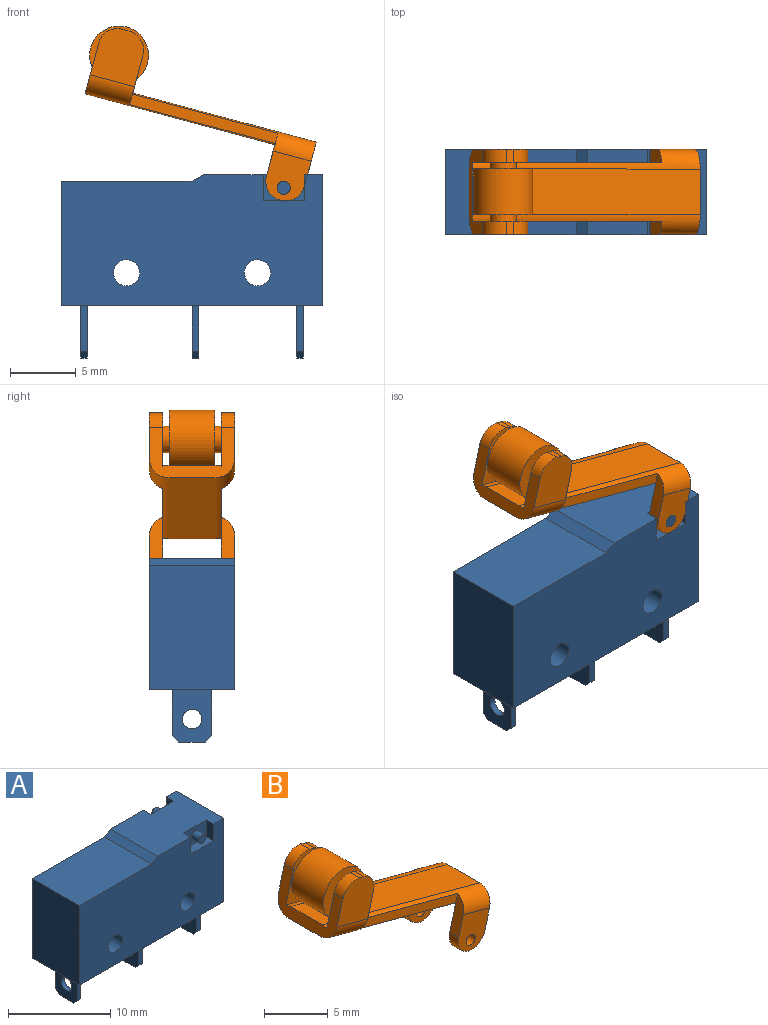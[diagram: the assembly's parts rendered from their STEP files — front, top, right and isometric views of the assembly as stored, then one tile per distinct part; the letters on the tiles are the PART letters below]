
ASSEMBLY  parts=2 mates=1
PART A: 46 faces, bbox 20x6.5x14 mm
  f0: plane 20x10mm, normal (0,1,0), area 182.2mm2, adj f2,f3,f4,f5,f6,f7,f8,f9
  f1: plane 20x10mm, normal (0,-1,0), area 182.2mm2, adj f2,f3,f4,f5,f6,f7,f8,f9
  f2: plane 20x6.5mm, normal (0,0,-1), area 125.5mm2, adj f0,f1,f6,f9,f10,f12,f13,f14
  f3: plane 9.13x6.5mm, normal (0,0,1), area 53.1mm2, adj f0,f1,f4,f9,f34,f35,f38,f40
  f4: plane 6.5x0.87mm, normal (-0.5,0,0.87), area 6.5mm2, adj f0,f1,f3,f5
  f5: plane 10x6.5mm, normal (0,0,1), area 65mm2, adj f0,f1,f4,f6
  f6: plane 9.5x6.5mm, normal (-1,0,0), area 61.8mm2, adj f0,f1,f2,f5
  f7: cylinder r=1mm len=6.5mm, axis (0,1,0), area 40.8mm2, adj f0,f1
  f8: cylinder r=1mm len=6.5mm, axis (0,1,0), area 40.8mm2, adj f0,f1
  f9: plane 10x6.5mm, normal (1,0,0), area 65mm2, adj f0,f1,f2,f3
  f10: plane 4x3mm, normal (-1,0,0), area 10mm2, adj f2,f11,f13,f14,f27,f30,f33
  f11: plane 2x0.5mm, normal (0,0,-1), area 1mm2, adj f10,f12,f30,f33
  f12: plane 4x3mm, normal (1,0,0), area 10mm2, adj f2,f11,f13,f14,f27,f30,f33
  f13: plane 3.5x0.5mm, normal (0,-1,0), area 1.8mm2, adj f2,f10,f12,f33
  f14: plane 3.5x0.5mm, normal (0,1,0), area 1.8mm2, adj f2,f10,f12,f30
  f15: plane 4x3mm, normal (-1,0,0), area 10mm2, adj f2,f16,f18,f19,f26,f29,f32
  f16: plane 2x0.5mm, normal (0,0,-1), area 1mm2, adj f15,f17,f29,f32
  f17: plane 4x3mm, normal (1,0,0), area 10mm2, adj f2,f16,f18,f19,f26,f29,f32
  f18: plane 3.5x0.5mm, normal (0,-1,0), area 1.8mm2, adj f2,f15,f17,f32
  f19: plane 3.5x0.5mm, normal (0,1,0), area 1.8mm2, adj f2,f15,f17,f29
  f20: plane 4x3mm, normal (-1,0,0), area 10mm2, adj f2,f21,f23,f24,f25,f28,f31
  f21: plane 2x0.5mm, normal (0,0,-1), area 1mm2, adj f20,f22,f28,f31
  f22: plane 4x3mm, normal (1,0,0), area 10mm2, adj f2,f21,f23,f24,f25,f28,f31
  f23: plane 3.5x0.5mm, normal (0,-1,0), area 1.8mm2, adj f2,f20,f22,f31
  f24: plane 3.5x0.5mm, normal (0,1,0), area 1.8mm2, adj f2,f20,f22,f28
  f25: cylinder r=0.75mm len=1.5mm, axis (-1,0,0), area 2.4mm2, adj f20,f22
  f26: cylinder r=0.75mm len=1.5mm, axis (-1,0,0), area 2.4mm2, adj f15,f17
  f27: cylinder r=0.75mm len=1.5mm, axis (-1,0,0), area 2.4mm2, adj f10,f12
  f28: plane 0.5x0.5mm, normal (0,0.71,-0.71), area 0.4mm2, adj f20,f21,f22,f24
  f29: plane 0.5x0.5mm, normal (0,0.71,-0.71), area 0.4mm2, adj f15,f16,f17,f19
  f30: plane 0.5x0.5mm, normal (0,0.71,-0.71), area 0.4mm2, adj f10,f11,f12,f14
  f31: plane 0.5x0.5mm, normal (0,-0.71,-0.71), area 0.4mm2, adj f20,f21,f22,f23
  f32: plane 0.5x0.5mm, normal (0,-0.71,-0.71), area 0.4mm2, adj f15,f16,f17,f18
  f33: plane 0.5x0.5mm, normal (0,-0.71,-0.71), area 0.4mm2, adj f10,f11,f12,f13
  f34: plane 2x1mm, normal (-1,0,0), area 2mm2, adj f1,f3,f37,f38
  f35: plane 2x1mm, normal (1,0,0), area 2mm2, adj f1,f3,f37,f38
  f36: cylinder r=0.5mm len=1mm, axis (0,-1,0), area 3.1mm2, adj f38,f39
  f37: plane 3.13x1mm, normal (0,0,1), area 3.1mm2, adj f1,f34,f35,f38
  f38: plane 3.13x2mm, normal (0,-1,0), area 5.5mm2, adj f3,f34,f35,f36,f37
  f39: plane 1x1mm, normal (0,-1,0), area 0.8mm2, adj f36
  f40: plane 2x1mm, normal (-1,0,0), area 2mm2, adj f0,f3,f41,f44
  f41: plane 3.13x1mm, normal (0,0,1), area 3.1mm2, adj f0,f40,f42,f44
  f42: plane 2x1mm, normal (1,0,0), area 2mm2, adj f0,f3,f41,f44
  f43: cylinder r=0.5mm len=1mm, axis (0,1,0), area 3.1mm2, adj f44,f45
  f44: plane 3.13x2mm, normal (0,1,0), area 5.5mm2, adj f3,f40,f41,f42,f43
  f45: plane 1x1mm, normal (0,1,0), area 0.8mm2, adj f43
PART B: 37 faces, bbox 17.9x6.5x13.4 mm
  f0: plane 11.32x3.78mm, normal (0,1,0), area 9.5mm2, adj f1,f15,f30,f33
  f1: plane 3.3x1mm, normal (-0.97,0,0.26), area 3mm2, adj f0,f2,f4,f33,f36
  f2: plane 4.39x3.62mm, normal (0,-1,0), area 10.5mm2, adj f1,f3,f5,f30,f36
  f3: plane 6.5x3.38mm, normal (0.97,0,-0.26), area 10.5mm2, adj f2,f4,f6,f8,f9,f13,f27,f30
  f4: plane 3.82x3.47mm, normal (0,1,0), area 8.7mm2, adj f1,f3,f5,f33,f36
  f5: cylinder r=0.5mm len=1mm, axis (0,-1,0), area 3.1mm2, adj f2,f4
  f6: plane 17.39x4.66mm, normal (-0.26,0,-0.97), area 63mm2, adj f3,f11,f27,f30
  f7: plane 3.3x1mm, normal (-0.97,0,0.26), area 3mm2, adj f8,f9,f12,f34,f35
  f8: plane 3.82x3.47mm, normal (0,-1,0), area 8.7mm2, adj f3,f7,f10,f34,f35
  f9: plane 4.39x3.62mm, normal (0,1,0), area 10.5mm2, adj f3,f7,f10,f27,f35
  f10: cylinder r=0.5mm len=1mm, axis (0,-1,0), area 3.1mm2, adj f8,f9
  f11: plane 6.5x3.86mm, normal (-0.97,0,0.26), area 11.5mm2, adj f6,f13,f14,f16,f18,f20,f27,f29
  f12: plane 11.32x3.78mm, normal (0,-1,0), area 9.5mm2, adj f7,f19,f27,f34
  f13: plane 17.39x4.66mm, normal (0.26,0,0.97), area 63mm2, adj f3,f11,f33,f34
  f14: plane 5x4.23mm, normal (0,-1,0), area 11.9mm2, adj f11,f15,f17,f25,f31,f32,f33
  f15: plane 3.78x1.01mm, normal (0.97,0,-0.26), area 3.5mm2, adj f0,f14,f16,f30,f32
  f16: plane 4.43x4.08mm, normal (0,1,0), area 13mm2, adj f11,f15,f17,f30,f31,f32
  f17: plane 1x0.48mm, normal (0.26,0,0.97), area 0.5mm2, adj f14,f16,f31,f32
  f18: plane 5x4.23mm, normal (0,1,0), area 11.9mm2, adj f11,f19,f21,f26,f28,f29,f34
  f19: plane 3.78x1.01mm, normal (0.97,0,-0.26), area 3.5mm2, adj f12,f18,f20,f27,f28
  f20: plane 4.43x4.08mm, normal (0,-1,0), area 13mm2, adj f11,f19,f21,f27,f28,f29
  f21: plane 1x0.48mm, normal (0.26,0,0.97), area 0.5mm2, adj f18,f20,f28,f29
  f22: plane 4.5x4.5mm, normal (0,-1,0), area 12.8mm2, adj f23,f26
  f23: cylinder r=2.25mm len=4.5mm, axis (0,1,0), area 49.5mm2, adj f22,f24
  f24: plane 4.5x4.5mm, normal (0,1,0), area 12.8mm2, adj f23,f25
  f25: cylinder r=1mm len=2mm, axis (0,1,0), area 3.1mm2, adj f14,f24
  f26: cylinder r=1mm len=2mm, axis (0,1,0), area 3.1mm2, adj f18,f22
  f27: cylinder r=1.5mm len=17.78mm, axis (0.97,0,-0.26), area 15.6mm2, adj f3,f6,f9,f11,f12,f19,f20
  f28: cylinder r=1.5mm len=1.84mm, axis (0,1,0), area 2.4mm2, adj f18,f19,f20,f21
  f29: cylinder r=1.5mm len=1.84mm, axis (0,-1,0), area 2.4mm2, adj f11,f18,f20,f21
  f30: cylinder r=1.5mm len=17.78mm, axis (-0.97,0,0.26), area 15.6mm2, adj f0,f2,f3,f6,f11,f15,f16
  f31: cylinder r=1.5mm len=1.84mm, axis (0,1,0), area 2.4mm2, adj f11,f14,f16,f17
  f32: cylinder r=1.5mm len=1.84mm, axis (0,1,0), area 2.4mm2, adj f14,f15,f16,f17
  f33: cylinder r=1.5mm len=17.78mm, axis (0.97,0,-0.26), area 14.7mm2, adj f0,f1,f3,f4,f11,f13,f14
  f34: cylinder r=1.5mm len=17.78mm, axis (0.97,0,-0.26), area 14.7mm2, adj f3,f7,f8,f11,f12,f13,f18
  f35: cylinder r=1.5mm len=2.95mm, axis (0,-1,0), area 4.7mm2, adj f3,f7,f8,f9
  f36: cylinder r=1.5mm len=2.95mm, axis (0,-1,0), area 4.7mm2, adj f1,f2,f3,f4
PLACE A t=(-1.14,3.99,1.17)mm fixed
PLACE B t=(-1.14,3.99,1.17)mm
MATE revolute A.f36 <-> B.f5  axis (0,1,0) through (5.86,6.74,5.17)mm
